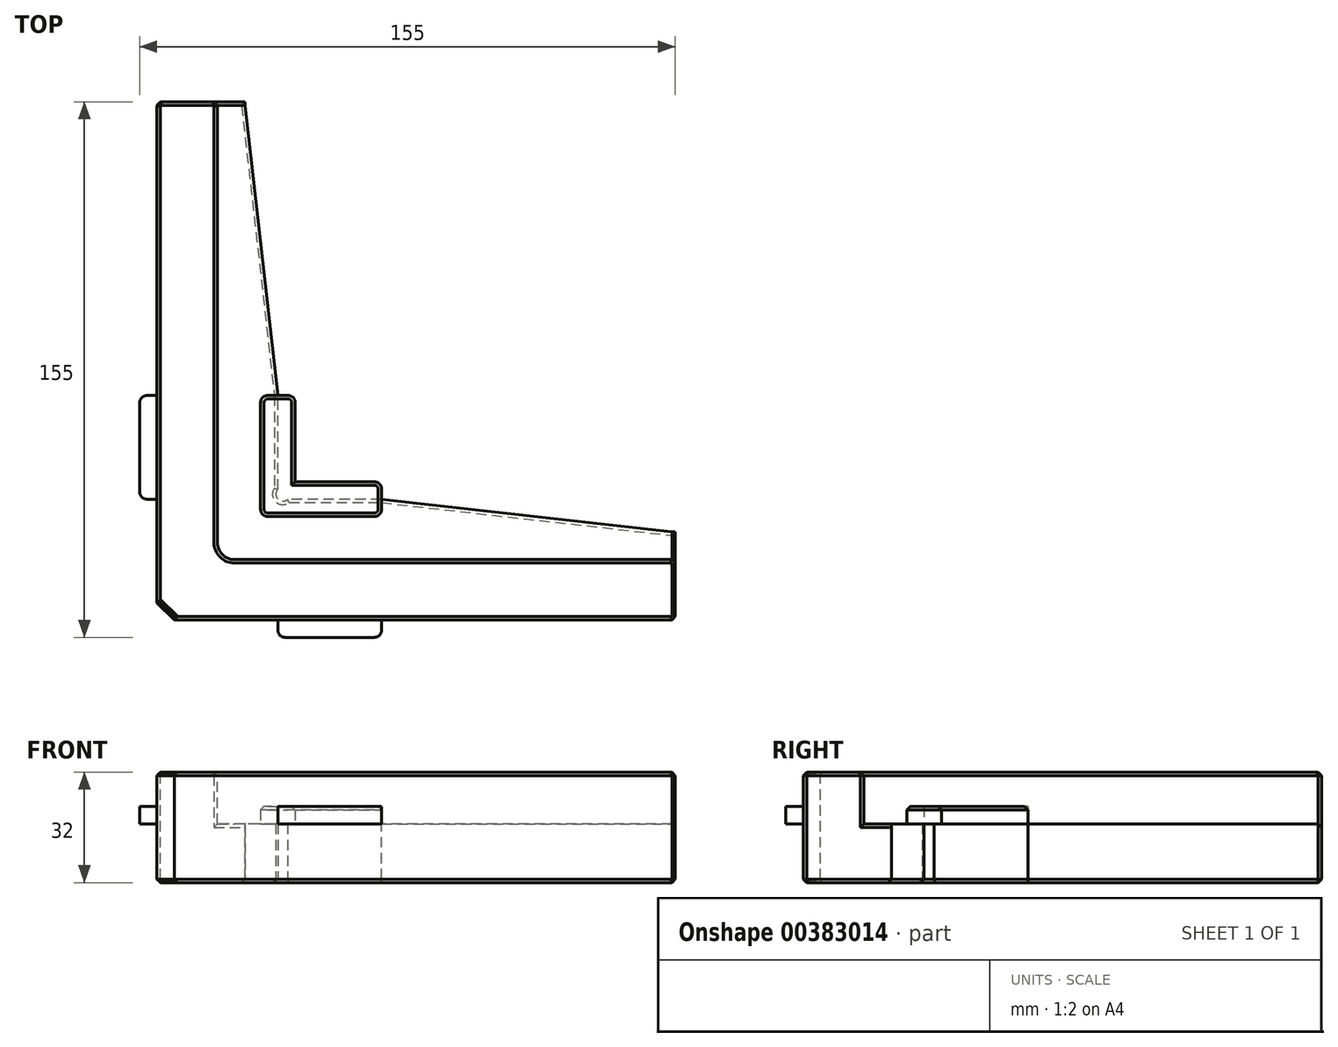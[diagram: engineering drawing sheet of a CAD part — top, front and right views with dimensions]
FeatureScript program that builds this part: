
annotation { "Feature Type Name" : "Feature", "Feature Type Description" : "" }
export const myFeature = defineFeature(function(context is Context, id is Id, definition is map)
    precondition{}
    {
        {
            var Q0;
            Q0=qCreatedBy(makeId("Top.planeOp"),FACE);
            var sketch = newSketch(context, id + "F0", { "sketchPlane" : qUnion([Q0])});
            skLineSegment(sketch, "E0", {"start": v(0, 0) * mm, "end": v(0, 150) * mm});
            skLineSegment(sketch, "E1", {"start": v(0, 150) * mm, "end": v(35, 150) * mm});
            skLineSegment(sketch, "E2", {"start": v(35, 150) * mm, "end": v(35, 37.83) * mm});
            skLineSegment(sketch, "E3", {"start": v(37.83, 35) * mm, "end": v(150, 35) * mm});
            skLineSegment(sketch, "E4", {"start": v(150, 35) * mm, "end": v(150, 0) * mm});
            skLineSegment(sketch, "E5", {"start": v(150, 0) * mm, "end": v(0, 0) * mm});
            skLineSegment(sketch, "E6", {"start": v(35, 35) * mm, "end": v(98.6, 98.6) * mm, "construction": true});
            skArc(sketch, "E7", {"start": v(35, 37.83) * mm, "mid": v(35, 35) * mm, "end": v(37.83, 35) * mm});
            skSolve(sketch);
        }
        {
            var Q0;
            Q0 = qSketchRegion(id + "F0", true);
            extrude(context, id + "F1", {"entities" : qUnion([Q0]), "offsetDistance" : 25 * mm, "depth" : 15 * mm});
        }
        {
            var Q0;
            Q0=makeQuery(id+"F1.opExtrude","CAP_FACE",FACE,{"disambiguationData":[OSD([sQuery(id+"F0.wireOp",EDGE,"E0"),sQuery(id+"F0.wireOp",EDGE,"E1"),sQuery(id+"F0.wireOp",EDGE,"E2"),sQuery(id+"F0.wireOp",EDGE,"E3"),sQuery(id+"F0.wireOp",EDGE,"E4"),sQuery(id+"F0.wireOp",EDGE,"E5"),sQuery(id+"F0.wireOp",EDGE,"E7")])],"isStart":false});
            var sketch = newSketch(context, id + "F2", { "sketchPlane" : qUnion([Q0])});
            skLineSegment(sketch, "E8.0.0", {"start": v(150, 0) * mm, "end": v(150, 35) * mm});
            skLineSegment(sketch, "E8.0.1", {"start": v(150, 35) * mm, "end": v(37.83, 35) * mm});
            skArc(sketch, "E8.0.2", {"start": v(37.83, 35) * mm, "mid": v(35, 35) * mm, "end": v(35, 37.83) * mm});
            skLineSegment(sketch, "E8.0.3", {"start": v(35, 37.83) * mm, "end": v(35, 150) * mm});
            skLineSegment(sketch, "E8.0.4", {"start": v(35, 150) * mm, "end": v(0, 150) * mm});
            skLineSegment(sketch, "E8.0.5", {"start": v(0, 150) * mm, "end": v(0, 0) * mm});
            skLineSegment(sketch, "E8.0.6", {"start": v(0, 0) * mm, "end": v(150, 0) * mm});
            skSolve(sketch);
        }
        {
            var Q0;
            Q0 = qSketchRegion(id + "F2", true);
            extrude(context, id + "F3", {"entities" : qUnion([Q0]), "operationType" : NewBodyOperationType.ADD, "depth" : 2 * mm});
        }
        {
            var Q0;
            Q0=makeQuery(id+"F3.opExtrude","CAP_FACE",FACE,{"disambiguationData":[OSD([sQuery(id+"F2.wireOp",EDGE,"E8.0.0"),sQuery(id+"F2.wireOp",EDGE,"E8.0.1"),sQuery(id+"F2.wireOp",EDGE,"E8.0.2"),sQuery(id+"F2.wireOp",EDGE,"E8.0.3"),sQuery(id+"F2.wireOp",EDGE,"E8.0.4"),sQuery(id+"F2.wireOp",EDGE,"E8.0.5"),sQuery(id+"F2.wireOp",EDGE,"E8.0.6")])],"isStart":false});
            var sketch = newSketch(context, id + "F4", { "sketchPlane" : qUnion([Q0])});
            skLineSegment(sketch, "E9.0.0", {"start": v(150, 0) * mm, "end": v(150, 35) * mm, "construction": true});
            skLineSegment(sketch, "E9.0.1", {"start": v(150, 35) * mm, "end": v(37.83, 35) * mm, "construction": true});
            skArc(sketch, "E9.0.2", {"start": v(37.83, 35) * mm, "mid": v(35, 35) * mm, "end": v(35, 37.83) * mm, "construction": true});
            skLineSegment(sketch, "E9.0.3", {"start": v(35, 37.83) * mm, "end": v(35, 150) * mm, "construction": true});
            skLineSegment(sketch, "E9.0.4", {"start": v(35, 150) * mm, "end": v(0, 150) * mm, "construction": true});
            skLineSegment(sketch, "E9.0.5", {"start": v(0, 150) * mm, "end": v(0, 0) * mm, "construction": true});
            skLineSegment(sketch, "E9.0.6", {"start": v(0, 0) * mm, "end": v(150, 0) * mm, "construction": true});
            skLineSegment(sketch, "E10.bottom", {"start": v(0, 150) * mm, "end": v(17.5, 150) * mm});
            skLineSegment(sketch, "E10.top", {"start": v(0, 0) * mm, "end": v(17.5, 0) * mm});
            skLineSegment(sketch, "E10.left", {"start": v(0, 150) * mm, "end": v(0, 0) * mm});
            skLineSegment(sketch, "E10.right", {"start": v(17.5, 150) * mm, "end": v(17.5, 0) * mm});
            skLineSegment(sketch, "E11.bottom", {"start": v(150, 0) * mm, "end": v(17.5, 0) * mm});
            skLineSegment(sketch, "E11.top", {"start": v(150, 17.5) * mm, "end": v(17.5, 17.5) * mm});
            skLineSegment(sketch, "E11.left", {"start": v(150, 0) * mm, "end": v(150, 17.5) * mm});
            skLineSegment(sketch, "E11.right", {"start": v(17.5, 0) * mm, "end": v(17.5, 17.5) * mm});
            skSolve(sketch);
        }
        {
            var Q0;
            Q0 = qSketchRegion(id + "F4", true);
            extrude(context, id + "F5", {"entities" : qUnion([Q0]), "operationType" : NewBodyOperationType.ADD, "depth" : 15 * mm});
        }
        {
            var Q0;
            Q0=makeQuery(id+"F3.opExtrude","CAP_FACE",FACE,{"disambiguationData":[OSD([sQuery(id+"F2.wireOp",EDGE,"E8.0.0"),sQuery(id+"F2.wireOp",EDGE,"E8.0.1"),sQuery(id+"F2.wireOp",EDGE,"E8.0.2"),sQuery(id+"F2.wireOp",EDGE,"E8.0.3"),sQuery(id+"F2.wireOp",EDGE,"E8.0.4"),sQuery(id+"F2.wireOp",EDGE,"E8.0.5"),sQuery(id+"F2.wireOp",EDGE,"E8.0.6")])],"isStart":false});
            var sketch = newSketch(context, id + "F6", { "sketchPlane" : qUnion([Q0])});
            skLineSegment(sketch, "E12.bottom", {"start": v(65, 35) * mm, "end": v(189.1, 35) * mm});
            skLineSegment(sketch, "E12.top", {"start": v(148.96, 25.5) * mm, "end": v(189.1, 25.5) * mm});
            skLineSegment(sketch, "E12.right", {"start": v(189.1, 35) * mm, "end": v(189.1, 25.5) * mm});
            skLineSegment(sketch, "E13.bottom", {"start": v(25.5, 166.87) * mm, "end": v(35, 166.87) * mm});
            skLineSegment(sketch, "E13.left", {"start": v(25.5, 166.87) * mm, "end": v(25.5, 148.96) * mm});
            skLineSegment(sketch, "E13.right", {"start": v(35, 166.87) * mm, "end": v(35, 65) * mm});
            skLineSegment(sketch, "E14", {"start": v(35, 65) * mm, "end": v(25.5, 148.96) * mm});
            skLineSegment(sketch, "E15", {"start": v(65, 35) * mm, "end": v(148.96, 25.5) * mm});
            skSolve(sketch);
        }
        {
            var Q0;
            Q0 = qSketchRegion(id + "F6", true);
            extrude(context, id + "F7", {"entities" : qUnion([Q0]), "operationType" : NewBodyOperationType.REMOVE, "endBound" : BoundingType.UP_TO_NEXT, "oppositeDirection" : true, "depth" : 25 * mm});
        }
        {
            var Q0;
            Q0=makeQuery(id+"F3.opExtrude","CAP_FACE",FACE,{"disambiguationData":[OSD([sQuery(id+"F2.wireOp",EDGE,"E8.0.0"),sQuery(id+"F2.wireOp",EDGE,"E8.0.1"),sQuery(id+"F2.wireOp",EDGE,"E8.0.2"),sQuery(id+"F2.wireOp",EDGE,"E8.0.3"),sQuery(id+"F2.wireOp",EDGE,"E8.0.4"),sQuery(id+"F2.wireOp",EDGE,"E8.0.5"),sQuery(id+"F2.wireOp",EDGE,"E8.0.6")])],"isStart":false});
            var sketch = newSketch(context, id + "F8", { "sketchPlane" : qUnion([Q0])});
            skLineSegment(sketch, "E16.bottom", {"start": v(35, 65) * mm, "end": v(40, 65) * mm});
            skLineSegment(sketch, "E16.top", {"start": v(35, 35) * mm, "end": v(40, 35) * mm});
            skLineSegment(sketch, "E16.left", {"start": v(35, 65) * mm, "end": v(35, 35) * mm});
            skLineSegment(sketch, "E16.right", {"start": v(40, 65) * mm, "end": v(40, 35) * mm});
            skLineSegment(sketch, "E17.bottom", {"start": v(65, 35) * mm, "end": v(40, 35) * mm});
            skLineSegment(sketch, "E17.top", {"start": v(65, 40) * mm, "end": v(40, 40) * mm});
            skLineSegment(sketch, "E17.left", {"start": v(65, 35) * mm, "end": v(65, 40) * mm});
            skLineSegment(sketch, "E17.right", {"start": v(40, 35) * mm, "end": v(40, 40) * mm});
            skLineSegment(sketch, "E18.bottom", {"start": v(0, 65) * mm, "end": v(-5, 65) * mm});
            skLineSegment(sketch, "E18.top", {"start": v(0, 35) * mm, "end": v(-5, 35) * mm});
            skLineSegment(sketch, "E18.left", {"start": v(0, 65) * mm, "end": v(0, 35) * mm});
            skLineSegment(sketch, "E18.right", {"start": v(-5, 65) * mm, "end": v(-5, 35) * mm});
            skLineSegment(sketch, "E19.bottom", {"start": v(35, 0) * mm, "end": v(65, 0) * mm});
            skLineSegment(sketch, "E19.top", {"start": v(35, -5) * mm, "end": v(65, -5) * mm});
            skLineSegment(sketch, "E19.left", {"start": v(35, 0) * mm, "end": v(35, -5) * mm});
            skLineSegment(sketch, "E19.right", {"start": v(65, 0) * mm, "end": v(65, -5) * mm});
            skLineSegment(sketch, "E20", {"start": v(35, 65) * mm, "end": v(30, 65) * mm});
            skLineSegment(sketch, "E21", {"start": v(30, 65) * mm, "end": v(30, 30) * mm});
            skLineSegment(sketch, "E22", {"start": v(30, 30) * mm, "end": v(65, 30) * mm});
            skLineSegment(sketch, "E23", {"start": v(65, 30) * mm, "end": v(65, 35) * mm});
            skSolve(sketch);
        }
        {
            var Q0;
            Q0 = qSketchRegion(id + "F8", true);
            extrude(context, id + "F9", {"entities" : qUnion([Q0]), "operationType" : NewBodyOperationType.ADD, "depth" : 5 * mm});
        }
        {
            var Q0;
            Q0=makeQuery(id+"F5.boolean.opBoolean","MERGE",EDGE,{"derivedFrom":[makeQuery(id+"F3.boolean.opBoolean","MERGE",EDGE,{"derivedFrom":[makeQuery(id+"F1.opExtrude","SWEPT_EDGE",EDGE,{"disambiguationData":[OSD([sQuery(id+"F0.wireOp",EDGE,"E4"),sQuery(id+"F0.wireOp",EDGE,"E5")])]}),makeQuery(id+"F3.opExtrude","SWEPT_EDGE",EDGE,{"disambiguationData":[OSD([sQuery(id+"F2.wireOp",EDGE,"E8.0.0"),sQuery(id+"F2.wireOp",EDGE,"E8.0.6")])]})]}),makeQuery(id+"F5.opExtrude","SWEPT_EDGE",EDGE,{"disambiguationData":[OSD([sQuery(id+"F4.wireOp",EDGE,"E11.bottom"),sQuery(id+"F4.wireOp",EDGE,"E11.left")])]})]});
            var Q1;
            Q1=makeQuery(id+"F5.opExtrude","SWEPT_EDGE",EDGE,{"disambiguationData":[OSD([sQuery(id+"F2.wireOp",EDGE,"E8.0.0"),sQuery(id+"F4.wireOp",EDGE,"E11.top"),sQuery(id+"F4.wireOp",EDGE,"E11.left")])]});
            var Q2;
            Q2=makeQuery(id+"F3.opExtrude","CAP_EDGE",EDGE,{"disambiguationData":[OSD([sQuery(id+"F2.wireOp",EDGE,"E8.0.0")])],"isStart":false});
            var Q3;
            {var subQ0=sQuery(id+"F2.wireOp",EDGE,"E8.0.0");var subQ1=sQuery(id+"F6.wireOp",EDGE,"E12.top");Q3=makeQuery(id+"F7.boolean.opBoolean","COPY",EDGE,{"derivedFrom":makeQuery(id+"F7.opExtrude","CAP_EDGE",EDGE,{"disambiguationData":[OSD([subQ1]),topologyDisambiguationEdgeConnected([makeQuery(id+"F5.boolean.opBoolean","MERGE",FACE,{"derivedFrom":[makeQuery(id+"F3.boolean.opBoolean","MERGE",FACE,{"derivedFrom":[makeQuery(id+"F1.opExtrude","SWEPT_FACE",FACE,{"disambiguationData":[OSD([sQuery(id+"F0.wireOp",EDGE,"E4")])]}),makeQuery(id+"F3.opExtrude","SWEPT_FACE",FACE,{"disambiguationData":[OSD([subQ0])]})]}),makeQuery(id+"F5.opExtrude","SWEPT_FACE",FACE,{"disambiguationData":[OSD([sQuery(id+"F4.wireOp",EDGE,"E11.left")])]})]})])],"isStart":false})});}
            var Q4;
            Q4=makeQuery(id+"F5.boolean.opBoolean","MERGE",EDGE,{"derivedFrom":[makeQuery(id+"F3.boolean.opBoolean","MERGE",EDGE,{"derivedFrom":[makeQuery(id+"F1.opExtrude","SWEPT_EDGE",EDGE,{"disambiguationData":[OSD([sQuery(id+"F0.wireOp",EDGE,"E0"),sQuery(id+"F0.wireOp",EDGE,"E1")])]}),makeQuery(id+"F3.opExtrude","SWEPT_EDGE",EDGE,{"disambiguationData":[OSD([sQuery(id+"F2.wireOp",EDGE,"E8.0.4"),sQuery(id+"F2.wireOp",EDGE,"E8.0.5")])]})]}),makeQuery(id+"F5.opExtrude","SWEPT_EDGE",EDGE,{"disambiguationData":[OSD([sQuery(id+"F4.wireOp",EDGE,"E10.bottom"),sQuery(id+"F4.wireOp",EDGE,"E10.left")])]})]});
            var Q5;
            Q5=makeQuery(id+"F5.opExtrude","SWEPT_EDGE",EDGE,{"disambiguationData":[OSD([sQuery(id+"F2.wireOp",EDGE,"E8.0.4"),sQuery(id+"F4.wireOp",EDGE,"E10.bottom"),sQuery(id+"F4.wireOp",EDGE,"E10.right")])]});
            var Q6;
            Q6=makeQuery(id+"F3.opExtrude","CAP_EDGE",EDGE,{"disambiguationData":[OSD([sQuery(id+"F2.wireOp",EDGE,"E8.0.4")])],"isStart":false});
            var Q7;
            Q7=makeQuery(id+"F7.boolean.opBoolean","COPY",EDGE,{"derivedFrom":makeQuery(id+"F7.opExtrude","CAP_EDGE",EDGE,{"disambiguationData":[OSD([sQuery(id+"F6.wireOp",EDGE,"E13.left")]),topologyDisambiguationEdgeConnected([makeQuery(id+"F5.boolean.opBoolean","MERGE",FACE,{"derivedFrom":[makeQuery(id+"F3.boolean.opBoolean","MERGE",FACE,{"derivedFrom":[makeQuery(id+"F1.opExtrude","SWEPT_FACE",FACE,{"disambiguationData":[OSD([sQuery(id+"F0.wireOp",EDGE,"E1")])]}),makeQuery(id+"F3.opExtrude","SWEPT_FACE",FACE,{"disambiguationData":[OSD([sQuery(id+"F2.wireOp",EDGE,"E8.0.4")])]})]}),makeQuery(id+"F5.opExtrude","SWEPT_FACE",FACE,{"disambiguationData":[OSD([sQuery(id+"F4.wireOp",EDGE,"E10.bottom")])]})]})])],"isStart":false})});
            chamfer(context, id + "F10", {"entities" : qUnion([Q0, Q1, Q2, Q3, Q4, Q5, Q6, Q7]), "width" : 1 * mm, "tangentPropagation" : true});
        }
        {
            var Q0;
            Q0=makeQuery(id+"F5.boolean.opBoolean","MERGE",EDGE,{"derivedFrom":[makeQuery(id+"F3.boolean.opBoolean","MERGE",EDGE,{"derivedFrom":[makeQuery(id+"F1.opExtrude","SWEPT_EDGE",EDGE,{"disambiguationData":[OSD([sQuery(id+"F0.wireOp",EDGE,"E0"),sQuery(id+"F0.wireOp",EDGE,"E5")])]}),makeQuery(id+"F3.opExtrude","SWEPT_EDGE",EDGE,{"disambiguationData":[OSD([sQuery(id+"F2.wireOp",EDGE,"E8.0.5"),sQuery(id+"F2.wireOp",EDGE,"E8.0.6")])]})]}),makeQuery(id+"F5.opExtrude","SWEPT_EDGE",EDGE,{"disambiguationData":[OSD([sQuery(id+"F4.wireOp",EDGE,"E10.top"),sQuery(id+"F4.wireOp",EDGE,"E10.left")])]})]});
            chamfer(context, id + "F11", {"entities" : qUnion([Q0]), "width" : 5 * mm, "tangentPropagation" : true});
        }
        {
            var Q0;
            Q0=makeQuery(id+"F9.opExtrude","SWEPT_EDGE",EDGE,{"disambiguationData":[OSD([sQuery(id+"F8.wireOp",EDGE,"E17.top"),sQuery(id+"F8.wireOp",EDGE,"E17.left")])]});
            var Q1;
            Q1=makeQuery(id+"F9.opExtrude","SWEPT_EDGE",EDGE,{"disambiguationData":[OSD([sQuery(id+"F8.wireOp",EDGE,"E22"),sQuery(id+"F8.wireOp",EDGE,"E23")])]});
            var Q2;
            Q2=makeQuery(id+"F9.opExtrude","SWEPT_EDGE",EDGE,{"disambiguationData":[OSD([sQuery(id+"F8.wireOp",EDGE,"E21"),sQuery(id+"F8.wireOp",EDGE,"E22")])]});
            var Q3;
            Q3=makeQuery(id+"F9.opExtrude","SWEPT_EDGE",EDGE,{"disambiguationData":[OSD([sQuery(id+"F8.wireOp",EDGE,"E20"),sQuery(id+"F8.wireOp",EDGE,"E21")])]});
            var Q4;
            Q4=makeQuery(id+"F9.opExtrude","SWEPT_EDGE",EDGE,{"disambiguationData":[OSD([sQuery(id+"F8.wireOp",EDGE,"E16.bottom"),sQuery(id+"F8.wireOp",EDGE,"E16.right")])]});
            var Q5;
            Q5=makeQuery(id+"F9.opExtrude","SWEPT_EDGE",EDGE,{"disambiguationData":[OSD([sQuery(id+"F8.wireOp",EDGE,"E18.top"),sQuery(id+"F8.wireOp",EDGE,"E18.left")])]});
            var Q6;
            Q6=makeQuery(id+"F9.opExtrude","SWEPT_EDGE",EDGE,{"disambiguationData":[OSD([sQuery(id+"F8.wireOp",EDGE,"E18.top"),sQuery(id+"F8.wireOp",EDGE,"E18.right")])]});
            var Q7;
            Q7=makeQuery(id+"F9.opExtrude","SWEPT_EDGE",EDGE,{"disambiguationData":[OSD([sQuery(id+"F8.wireOp",EDGE,"E18.bottom"),sQuery(id+"F8.wireOp",EDGE,"E18.right")])]});
            var Q8;
            Q8=makeQuery(id+"F9.opExtrude","SWEPT_EDGE",EDGE,{"disambiguationData":[OSD([sQuery(id+"F8.wireOp",EDGE,"E18.bottom"),sQuery(id+"F8.wireOp",EDGE,"E18.left")])]});
            var Q9;
            Q9=makeQuery(id+"F9.opExtrude","SWEPT_EDGE",EDGE,{"disambiguationData":[OSD([sQuery(id+"F8.wireOp",EDGE,"E19.bottom"),sQuery(id+"F8.wireOp",EDGE,"E19.left")])]});
            var Q10;
            Q10=makeQuery(id+"F9.opExtrude","SWEPT_EDGE",EDGE,{"disambiguationData":[OSD([sQuery(id+"F8.wireOp",EDGE,"E19.top"),sQuery(id+"F8.wireOp",EDGE,"E19.left")])]});
            var Q11;
            Q11=makeQuery(id+"F9.opExtrude","SWEPT_EDGE",EDGE,{"disambiguationData":[OSD([sQuery(id+"F8.wireOp",EDGE,"E19.top"),sQuery(id+"F8.wireOp",EDGE,"E19.right")])]});
            var Q12;
            Q12=makeQuery(id+"F9.opExtrude","SWEPT_EDGE",EDGE,{"disambiguationData":[OSD([sQuery(id+"F8.wireOp",EDGE,"E19.bottom"),sQuery(id+"F8.wireOp",EDGE,"E19.right")])]});
            fillet(context, id + "F12", {"entities" : qUnion([Q0, Q1, Q2, Q3, Q4, Q5, Q6, Q7, Q8, Q9, Q10, Q11, Q12]), "radius" : 2 * mm, "tangentPropagation" : true, "allowEdgeOverflow" : false});
        }
        {
            var Q0;
            Q0=makeQuery(id+"F9.opExtrude","CAP_FACE",FACE,{"disambiguationData":[OSD([sQuery(id+"F8.wireOp",EDGE,"E16.bottom"),sQuery(id+"F8.wireOp",EDGE,"E16.right"),sQuery(id+"F8.wireOp",EDGE,"E17.top"),sQuery(id+"F8.wireOp",EDGE,"E17.left"),sQuery(id+"F8.wireOp",EDGE,"E20"),sQuery(id+"F8.wireOp",EDGE,"E21"),sQuery(id+"F8.wireOp",EDGE,"E22"),sQuery(id+"F8.wireOp",EDGE,"E23")])],"isStart":false});
            chamfer(context, id + "F13", {"entities" : qUnion([Q0]), "width" : 1 * mm, "tangentPropagation" : true});
        }
        {
            var Q0;
            {var subQ0=sQuery(id+"F4.wireOp",EDGE,"E10.left");var subQ1=sQuery(id+"F4.wireOp",EDGE,"E10.top");Q0=makeQuery(id+"F11.opChamfer","BLEND_EDGE",EDGE,{"blendedFrom":[makeQuery(id+"F5.boolean.opBoolean","MERGE",EDGE,{"derivedFrom":[makeQuery(id+"F3.boolean.opBoolean","MERGE",EDGE,{"derivedFrom":[makeQuery(id+"F1.opExtrude","SWEPT_EDGE",EDGE,{"disambiguationData":[OSD([sQuery(id+"F0.wireOp",EDGE,"E0"),sQuery(id+"F0.wireOp",EDGE,"E5")])]}),makeQuery(id+"F3.opExtrude","SWEPT_EDGE",EDGE,{"disambiguationData":[OSD([sQuery(id+"F2.wireOp",EDGE,"E8.0.5"),sQuery(id+"F2.wireOp",EDGE,"E8.0.6")])]})]}),makeQuery(id+"F5.opExtrude","SWEPT_EDGE",EDGE,{"disambiguationData":[OSD([subQ1,subQ0])]})]}),makeQuery(id+"F5.opExtrude","CAP_FACE",FACE,{"disambiguationData":[OSD([sQuery(id+"F4.wireOp",EDGE,"E10.bottom"),subQ1,subQ0,sQuery(id+"F4.wireOp",EDGE,"E10.right"),sQuery(id+"F4.wireOp",EDGE,"E11.bottom"),sQuery(id+"F4.wireOp",EDGE,"E11.top"),sQuery(id+"F4.wireOp",EDGE,"E11.left")])],"isStart":false})],"blendedInto":[makeQuery(id+"F5.opExtrude","CAP_FACE",FACE,{"disambiguationData":[OSD([sQuery(id+"F4.wireOp",EDGE,"E10.bottom"),subQ1,subQ0,sQuery(id+"F4.wireOp",EDGE,"E10.right"),sQuery(id+"F4.wireOp",EDGE,"E11.bottom"),sQuery(id+"F4.wireOp",EDGE,"E11.top"),sQuery(id+"F4.wireOp",EDGE,"E11.left")])],"isStart":false})]});}
            var Q1;
            {var subQ0=sQuery(id+"F0.wireOp",EDGE,"E5");var subQ1=sQuery(id+"F0.wireOp",EDGE,"E0");Q1=makeQuery(id+"F11.opChamfer","BLEND_EDGE",EDGE,{"blendedFrom":[makeQuery(id+"F5.boolean.opBoolean","MERGE",EDGE,{"derivedFrom":[makeQuery(id+"F3.boolean.opBoolean","MERGE",EDGE,{"derivedFrom":[makeQuery(id+"F1.opExtrude","SWEPT_EDGE",EDGE,{"disambiguationData":[OSD([subQ1,subQ0])]}),makeQuery(id+"F3.opExtrude","SWEPT_EDGE",EDGE,{"disambiguationData":[OSD([sQuery(id+"F2.wireOp",EDGE,"E8.0.5"),sQuery(id+"F2.wireOp",EDGE,"E8.0.6")])]})]}),makeQuery(id+"F5.opExtrude","SWEPT_EDGE",EDGE,{"disambiguationData":[OSD([sQuery(id+"F4.wireOp",EDGE,"E10.top"),sQuery(id+"F4.wireOp",EDGE,"E10.left")])]})]}),makeQuery(id+"F1.opExtrude","CAP_FACE",FACE,{"disambiguationData":[OSD([subQ1,sQuery(id+"F0.wireOp",EDGE,"E1"),sQuery(id+"F0.wireOp",EDGE,"E2"),sQuery(id+"F0.wireOp",EDGE,"E3"),sQuery(id+"F0.wireOp",EDGE,"E4"),subQ0,sQuery(id+"F0.wireOp",EDGE,"E7")])],"isStart":true})],"blendedInto":[makeQuery(id+"F1.opExtrude","CAP_FACE",FACE,{"disambiguationData":[OSD([subQ1,sQuery(id+"F0.wireOp",EDGE,"E1"),sQuery(id+"F0.wireOp",EDGE,"E2"),sQuery(id+"F0.wireOp",EDGE,"E3"),sQuery(id+"F0.wireOp",EDGE,"E4"),subQ0,sQuery(id+"F0.wireOp",EDGE,"E7")])],"isStart":true})]});}
            chamfer(context, id + "F14", {"entities" : qUnion([Q0, Q1]), "width" : 1 * mm, "tangentPropagation" : true});
        }
        {
            var Q0;
            Q0=makeQuery(id+"F5.opExtrude","SWEPT_EDGE",EDGE,{"disambiguationData":[OSD([sQuery(id+"F4.wireOp",EDGE,"E10.right"),sQuery(id+"F4.wireOp",EDGE,"E11.top"),sQuery(id+"F4.wireOp",EDGE,"E11.right")])]});
            fillet(context, id + "F15", {"entities" : qUnion([Q0]), "radius" : 5 * mm, "tangentPropagation" : true, "allowEdgeOverflow" : false});
        }
        {
            var Q0;
            Q0=makeQuery(id+"F5.opExtrude","CAP_FACE",FACE,{"disambiguationData":[OSD([sQuery(id+"F4.wireOp",EDGE,"E10.bottom"),sQuery(id+"F4.wireOp",EDGE,"E10.top"),sQuery(id+"F4.wireOp",EDGE,"E10.left"),sQuery(id+"F4.wireOp",EDGE,"E10.right"),sQuery(id+"F4.wireOp",EDGE,"E11.bottom"),sQuery(id+"F4.wireOp",EDGE,"E11.top"),sQuery(id+"F4.wireOp",EDGE,"E11.left")])],"isStart":false});
            chamfer(context, id + "F16", {"entities" : qUnion([Q0]), "width" : 1 * mm, "tangentPropagation" : true});
        }
        {
            var Q0;
            Q0=makeQuery(id+"F1.opExtrude","CAP_FACE",FACE,{"disambiguationData":[OSD([sQuery(id+"F0.wireOp",EDGE,"E0"),sQuery(id+"F0.wireOp",EDGE,"E1"),sQuery(id+"F0.wireOp",EDGE,"E2"),sQuery(id+"F0.wireOp",EDGE,"E3"),sQuery(id+"F0.wireOp",EDGE,"E4"),sQuery(id+"F0.wireOp",EDGE,"E5"),sQuery(id+"F0.wireOp",EDGE,"E7")])],"isStart":true});
            chamfer(context, id + "F17", {"entities" : qUnion([Q0]), "width" : 1 * mm, "tangentPropagation" : true});
        }
    });
